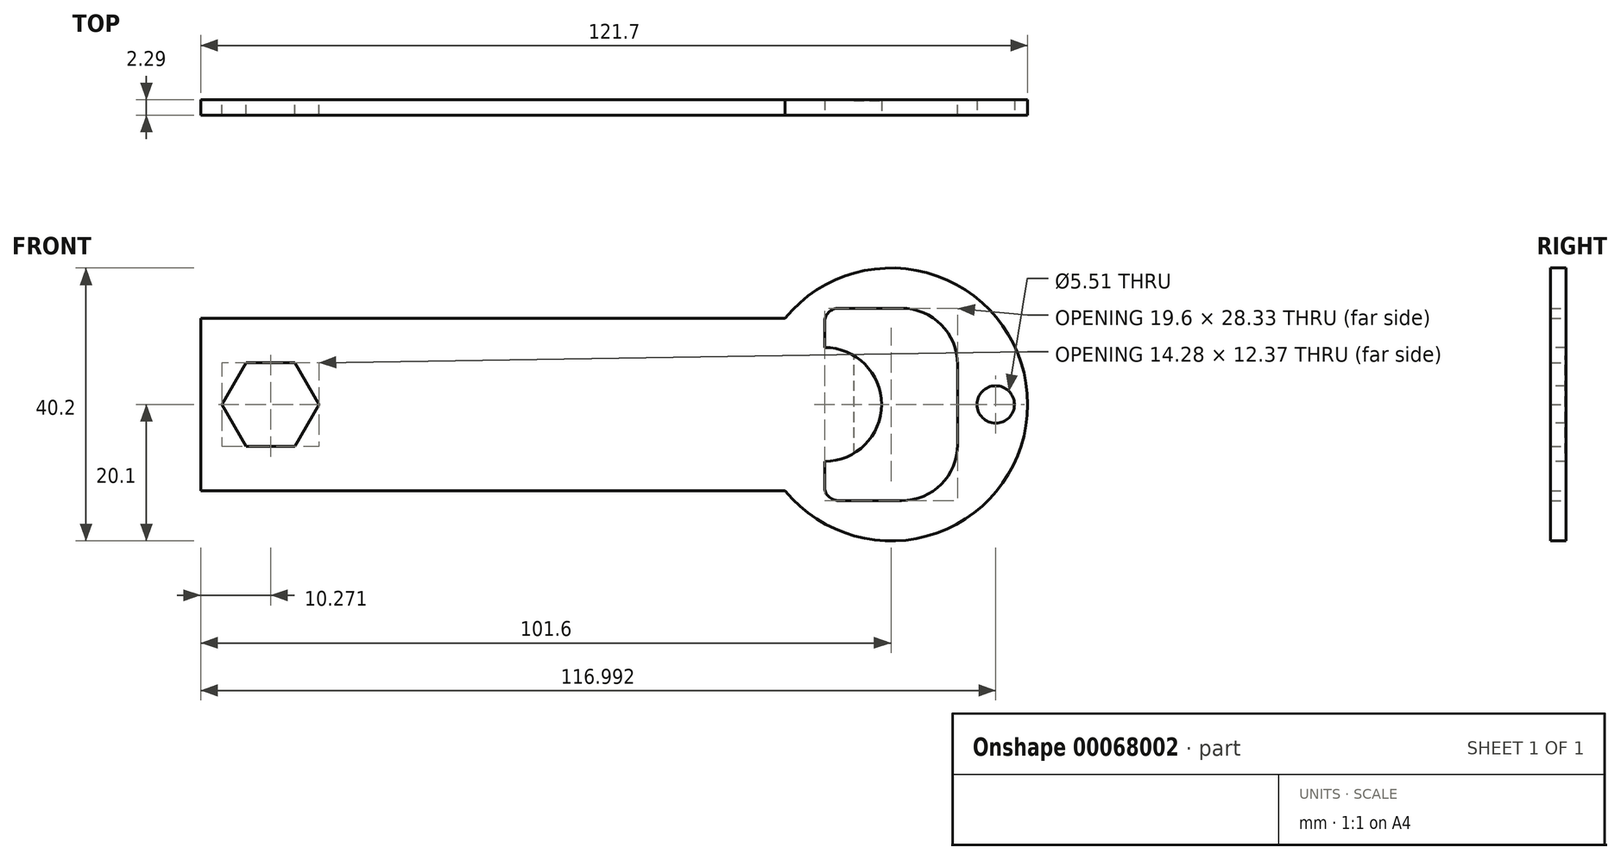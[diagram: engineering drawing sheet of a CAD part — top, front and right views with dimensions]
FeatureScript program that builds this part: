
annotation { "Feature Type Name" : "Feature", "Feature Type Description" : "" }
export const myFeature = defineFeature(function(context is Context, id is Id, definition is map)
    precondition{}
    {
        {
            var Q0;
            Q0=qCreatedBy(makeId("Front.planeOp"),FACE);
            var sketch = newSketch(context, id + "F0", { "sketchPlane" : qUnion([Q0])});
            skLineSegment(sketch, "E0.rect.bottom", {"start": v(50.8, -12.7) * mm, "end": v(-50.8, -12.7) * mm});
            skLineSegment(sketch, "E0.rect.top", {"start": v(50.8, 12.7) * mm, "end": v(-50.8, 12.7) * mm});
            skLineSegment(sketch, "E0.rect.left", {"start": v(50.8, -12.7) * mm, "end": v(50.8, 12.7) * mm});
            skLineSegment(sketch, "E0.rect.right", {"start": v(-50.8, -12.7) * mm, "end": v(-50.8, 12.7) * mm});
            skPoint(sketch, "E0.rect.middle", {"position": v(0, 0) * mm});
            skCircle(sketch, "E1", {"center": v(50.8, 0) * mm, "radius": 20.1 * mm});
            skLineSegment(sketch, "E2.rect.bottom", {"start": v(60.6, -14.17) * mm, "end": v(41, -14.17) * mm});
            skLineSegment(sketch, "E2.rect.top", {"start": v(60.6, 14.17) * mm, "end": v(41, 14.17) * mm});
            skLineSegment(sketch, "E2.rect.left", {"start": v(60.6, -14.17) * mm, "end": v(60.6, 14.17) * mm});
            skLineSegment(sketch, "E2.rect.right", {"start": v(41, -14.17) * mm, "end": v(41, 14.17) * mm});
            skSolve(sketch);
        }
        {
            var Q0;
            Q0=qCreatedBy(makeId("Front.planeOp"),FACE);
            var sketch = newSketch(context, id + "F1", { "sketchPlane" : qUnion([Q0])});
            skSolve(sketch);
        }
        {
            var Q0;
            Q0 = qSketchRegion(id + "F1", true);
            var Q1;
            {var subQ0=sQuery(id+"F0.wireOp",EDGE,"E0.rect.right");Q1=makeQuery(id+"F0.imprint","IMPRINT",FACE,{"disambiguationData":[TD([[makeQuery(id+"F0.imprint","IMPRINT",EDGE,{"derivedFrom":subQ0}),-1.0]])]});}
            var Q2;
            {var subQ0=sQuery(id+"F0.wireOp",EDGE,"E2.rect.bottom");Q2=makeQuery(id+"F0.imprint","IMPRINT",FACE,{"disambiguationData":[TD([[makeQuery(id+"F0.imprint","IMPRINT",EDGE,{"derivedFrom":subQ0}),1.0]])]});}
            var Q3;
            {var subQ0=sQuery(id+"F0.wireOp",EDGE,"E1");var subQ1=sQuery(id+"F0.wireOp",EDGE,"E0.rect.bottom");var subQ2=makeQuery(id+"F0.imprint","INTERSECT",VERTEX,{"derivedFrom":[subQ1,subQ0]});Q3=makeQuery(id+"F0.imprint","IMPRINT",FACE,{"disambiguationData":[TD([[makeQuery(id+"F0.imprint","IMPRINT",EDGE,{"disambiguationData":[TD([[subQ2,1.0]])],"derivedFrom":subQ1}),-1.0]])]});}
            extrude(context, id + "F2", {"entities" : qUnion([Q0, Q1, Q2, Q3]), "depth" : 2.3 * mm});
        }
        {
            var Q0;
            Q0=makeQuery(id+"F2.opExtrude","CAP_FACE",FACE,{"disambiguationData":[OSD([sQuery(id+"F0.wireOp",EDGE,"E0.rect.bottom"),sQuery(id+"F0.wireOp",EDGE,"E0.rect.top"),sQuery(id+"F0.wireOp",EDGE,"E0.rect.right"),sQuery(id+"F0.wireOp",EDGE,"E1"),sQuery(id+"F0.wireOp",EDGE,"E2.rect.bottom"),sQuery(id+"F0.wireOp",EDGE,"E2.rect.top"),sQuery(id+"F0.wireOp",EDGE,"E2.rect.left"),sQuery(id+"F0.wireOp",EDGE,"E2.rect.right")])],"isStart":false});
            var sketch = newSketch(context, id + "F3", { "sketchPlane" : qUnion([Q0])});
            skArc(sketch, "E3", {"start": v(41, -8.4) * mm, "mid": v(49.4, 0) * mm, "end": v(41, 8.4) * mm});
            skSolve(sketch);
        }
        {
            var Q0;
            {var subQ0=sQuery(id+"F3.wireOp",EDGE,"E3");Q0=makeQuery(id+"F3.imprint","IMPRINT",FACE,{"disambiguationData":[TD([[makeQuery(id+"F3.imprint","IMPRINT",EDGE,{"derivedFrom":subQ0}),1.0]])]});}
            extrude(context, id + "F4", {"entities" : qUnion([Q0]), "operationType" : NewBodyOperationType.ADD, "oppositeDirection" : true, "depth" : 2.3 * mm});
        }
        {
            var Q0;
            Q0=makeQuery(id+"F2.opExtrude","SWEPT_EDGE",EDGE,{"disambiguationData":[OSD([sQuery(id+"F0.wireOp",EDGE,"E2.rect.top"),sQuery(id+"F0.wireOp",EDGE,"E2.rect.right")])]});
            var Q1;
            Q1=makeQuery(id+"F2.opExtrude","SWEPT_EDGE",EDGE,{"disambiguationData":[OSD([sQuery(id+"F0.wireOp",EDGE,"E2.rect.bottom"),sQuery(id+"F0.wireOp",EDGE,"E2.rect.right")])]});
            fillet(context, id + "F5", {"entities" : qUnion([Q0, Q1]), "radius" : 2.07 * mm, "tangentPropagation" : true, "allowEdgeOverflow" : false});
        }
        {
            var Q0;
            {var subQ0=sQuery(id+"F0.wireOp",EDGE,"E2.rect.right");Q0=makeQuery(id+"F4.boolean.opBoolean","MERGE",FACE,{"derivedFrom":[makeQuery(id+"F2.opExtrude","CAP_FACE",FACE,{"disambiguationData":[OSD([sQuery(id+"F0.wireOp",EDGE,"E0.rect.bottom"),sQuery(id+"F0.wireOp",EDGE,"E0.rect.top"),sQuery(id+"F0.wireOp",EDGE,"E0.rect.right"),sQuery(id+"F0.wireOp",EDGE,"E1"),sQuery(id+"F0.wireOp",EDGE,"E2.rect.bottom"),sQuery(id+"F0.wireOp",EDGE,"E2.rect.top"),sQuery(id+"F0.wireOp",EDGE,"E2.rect.left"),subQ0])],"isStart":true}),makeQuery(id+"F4.opExtrude","CAP_FACE",FACE,{"disambiguationData":[OSD([subQ0,sQuery(id+"F3.wireOp",EDGE,"E3")])],"isStart":false})]});}
            var sketch = newSketch(context, id + "F6", { "sketchPlane" : qUnion([Q0])});
            skSolve(sketch);
        }
        {
            var Q0;
            Q0=makeQuery(id+"F2.opExtrude","SWEPT_EDGE",EDGE,{"disambiguationData":[OSD([sQuery(id+"F0.wireOp",EDGE,"E2.rect.bottom"),sQuery(id+"F0.wireOp",EDGE,"E2.rect.left")])]});
            var Q1;
            Q1=makeQuery(id+"F2.opExtrude","SWEPT_EDGE",EDGE,{"disambiguationData":[OSD([sQuery(id+"F0.wireOp",EDGE,"E2.rect.top"),sQuery(id+"F0.wireOp",EDGE,"E2.rect.left")])]});
            fillet(context, id + "F7", {"entities" : qUnion([Q0, Q1]), "radius" : 8.27 * mm, "tangentPropagation" : true, "allowEdgeOverflow" : false});
        }
        {
            var Q0;
            {var subQ0=sQuery(id+"F0.wireOp",EDGE,"E2.rect.right");Q0=makeQuery(id+"F4.boolean.opBoolean","MERGE",FACE,{"derivedFrom":[makeQuery(id+"F2.opExtrude","CAP_FACE",FACE,{"disambiguationData":[OSD([sQuery(id+"F0.wireOp",EDGE,"E0.rect.bottom"),sQuery(id+"F0.wireOp",EDGE,"E0.rect.top"),sQuery(id+"F0.wireOp",EDGE,"E0.rect.right"),sQuery(id+"F0.wireOp",EDGE,"E1"),sQuery(id+"F0.wireOp",EDGE,"E2.rect.bottom"),sQuery(id+"F0.wireOp",EDGE,"E2.rect.top"),sQuery(id+"F0.wireOp",EDGE,"E2.rect.left"),subQ0])],"isStart":false}),makeQuery(id+"F4.opExtrude","CAP_FACE",FACE,{"disambiguationData":[OSD([subQ0,sQuery(id+"F3.wireOp",EDGE,"E3")])],"isStart":true})]});}
            var sketch = newSketch(context, id + "F8", { "sketchPlane" : qUnion([Q0])});
            skCircle(sketch, "E4", {"center": v(66.2, 0) * mm, "radius": 2.75 * mm});
            skSolve(sketch);
        }
        {
            var Q0;
            Q0=makeQuery(id+"F8.imprint","IMPRINT",FACE,{"disambiguationData":[TD([[makeQuery(id+"F8.imprint","IMPRINT",EDGE,{"derivedFrom":sQuery(id+"F8.wireOp",EDGE,"E4")}),1.0]])]});
            extrude(context, id + "F9", {"entities" : qUnion([Q0]), "operationType" : NewBodyOperationType.REMOVE, "oppositeDirection" : true, "depth" : 25.4 * mm});
        }
        {
            var Q0;
            {var subQ9=sQuery(id+"F0.wireOp",EDGE,"E0.rect.bottom");Q0=makeQuery(id+"F6.imprint","IMPRINT",FACE,{"disambiguationData":[TD([[makeQuery(id+"F6.imprint","IMPRINT",EDGE,{"derivedFrom":makeQuery(id+"F2.opExtrude","CAP_EDGE",EDGE,{"disambiguationData":[OSD([subQ9])],"isStart":true})}),1.0]])]});}
            var sketch = newSketch(context, id + "F10", { "sketchPlane" : qUnion([Q0])});
            skLineSegment(sketch, "E5.rect.bottom", {"start": v(-53.33, -8.2) * mm, "end": v(-45.33, -8.2) * mm});
            skLineSegment(sketch, "E5.rect.top", {"start": v(-53.33, 8.2) * mm, "end": v(-45.33, 8.2) * mm});
            skLineSegment(sketch, "E5.rect.left", {"start": v(-53.33, -8.2) * mm, "end": v(-53.33, 8.2) * mm});
            skLineSegment(sketch, "E5.rect.right", {"start": v(-45.33, -8.2) * mm, "end": v(-45.33, 8.2) * mm});
            skPoint(sketch, "E5.rect.middle", {"position": v(-49.33, 0) * mm});
            skSolve(sketch);
        }
        {
            var Q0;
            {var subQ0=sQuery(id+"F10.wireOp",EDGE,"E5.rect.right");var subQ1=makeQuery(id+"F6.imprint","IMPRINT",EDGE,{"derivedFrom":makeQuery(id+"F4.opExtrude","CAP_EDGE",EDGE,{"disambiguationData":[OSD([sQuery(id+"F3.wireOp",EDGE,"E3")])],"isStart":false})});var subQ2=makeQuery(id+"F10.imprint","INTERSECT",VERTEX,{"disambiguationData":[OD(0.0)],"derivedFrom":[subQ1,subQ0]});Q0=makeQuery(id+"F10.imprint","IMPRINT",FACE,{"disambiguationData":[TD([[makeQuery(id+"F10.imprint","IMPRINT",EDGE,{"disambiguationData":[TD([[subQ2,-1.0]])],"derivedFrom":subQ0}),1.0]])]});}
            var Q1;
            Q1=sQuery(id+"F10.wireOp",EDGE,"E5.rect.top");
            var Q2;
            Q2=sQuery(id+"F10.wireOp",EDGE,"E5.rect.right");
            var Q3;
            Q3=sQuery(id+"F10.wireOp",EDGE,"E5.rect.bottom");
            var Q4;
            Q4=sQuery(id+"F10.wireOp",EDGE,"E5.rect.left");
            extrude(context, id + "F11", {"entities" : qUnion([Q0]), "operationType" : NewBodyOperationType.REMOVE, "surfaceEntities" : qUnion([Q1, Q2, Q3, Q4]), "oppositeDirection" : true, "depth" : 0.13 * mm});
        }
        {
            var Q0;
            {var subQ9=sQuery(id+"F0.wireOp",EDGE,"E0.rect.bottom");Q0=makeQuery(id+"F6.imprint","IMPRINT",FACE,{"disambiguationData":[TD([[makeQuery(id+"F6.imprint","IMPRINT",EDGE,{"derivedFrom":makeQuery(id+"F2.opExtrude","CAP_EDGE",EDGE,{"disambiguationData":[OSD([subQ9])],"isStart":true})}),1.0]])]});}
            var sketch = newSketch(context, id + "F12", { "sketchPlane" : qUnion([Q0])});
            skCircle(sketch, "E6.cCircle", {"center": v(40.53, 0) * mm, "radius": 6.18 * mm, "construction": true});
            skLineSegment(sketch, "E6.0", {"start": v(36.96, 6.18) * mm, "end": v(44.1, 6.18) * mm});
            skLineSegment(sketch, "E6.1", {"start": v(44.1, 6.18) * mm, "end": v(47.67, 0) * mm});
            skLineSegment(sketch, "E6.2", {"start": v(47.67, 0) * mm, "end": v(44.1, -6.18) * mm});
            skLineSegment(sketch, "E6.3", {"start": v(44.1, -6.18) * mm, "end": v(36.96, -6.18) * mm});
            skLineSegment(sketch, "E6.4", {"start": v(36.96, -6.18) * mm, "end": v(33.39, 0) * mm});
            skLineSegment(sketch, "E6.5", {"start": v(33.39, 0) * mm, "end": v(36.96, 6.18) * mm});
            skPoint(sketch, "E6.0.midPoint", {"position": v(40.53, 6.18) * mm});
            skSolve(sketch);
        }
        {
            var Q0;
            Q0=makeQuery(id+"F12.imprint","IMPRINT",FACE,{"disambiguationData":[TD([[makeQuery(id+"F12.imprint","IMPRINT",EDGE,{"derivedFrom":sQuery(id+"F12.wireOp",EDGE,"E6.0")}),-1.0]])]});
            extrude(context, id + "F13", {"entities" : qUnion([Q0]), "operationType" : NewBodyOperationType.REMOVE, "oppositeDirection" : true, "depth" : 25.4 * mm});
        }
    });
